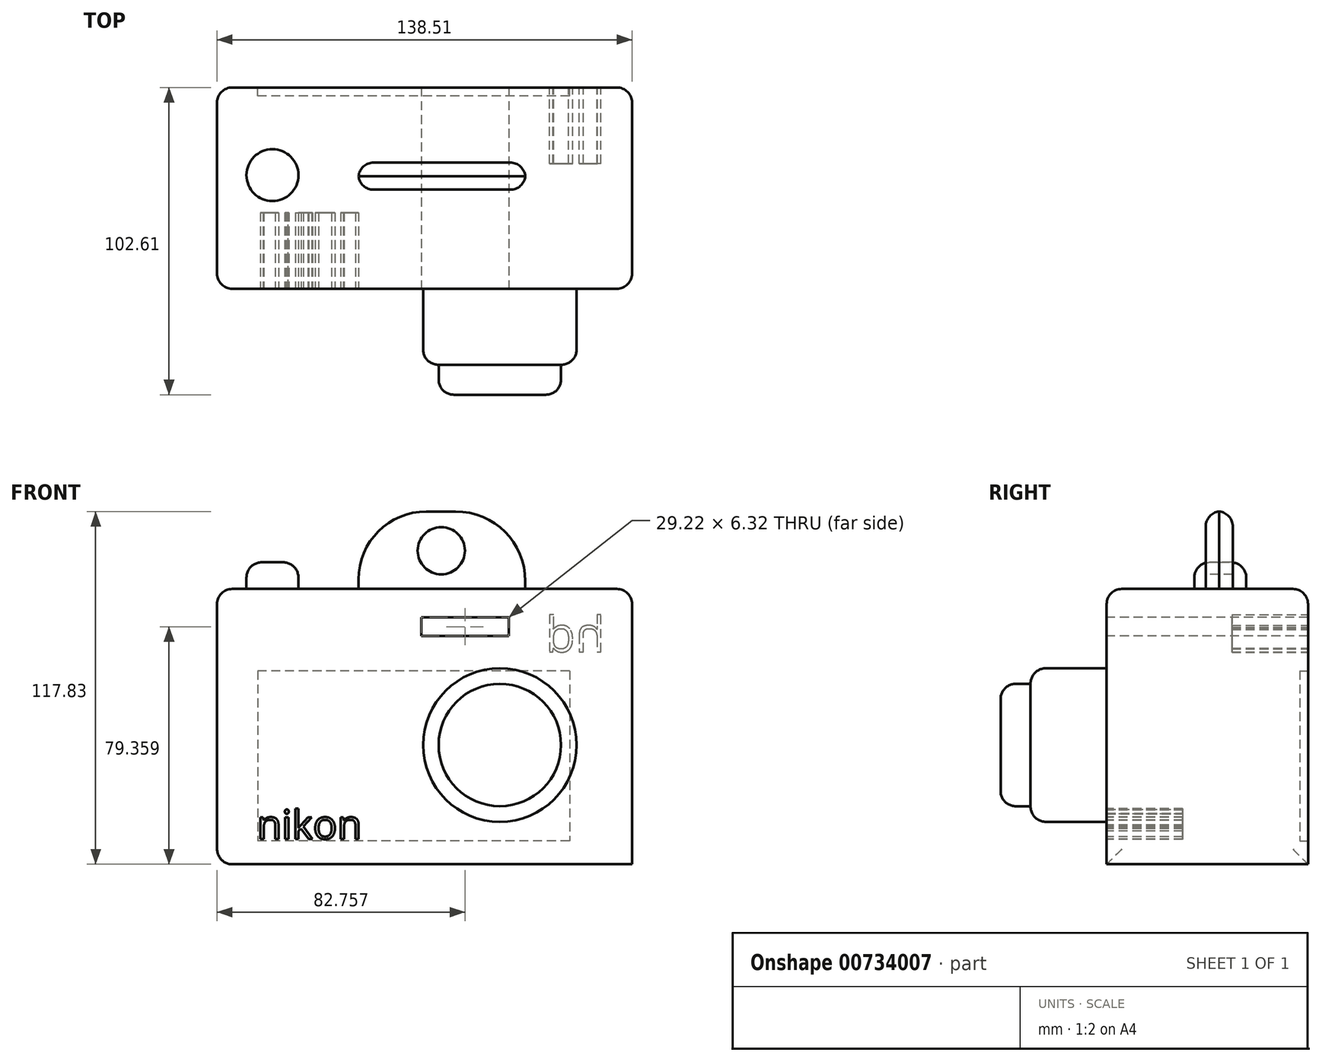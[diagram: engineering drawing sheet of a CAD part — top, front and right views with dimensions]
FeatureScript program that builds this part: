
annotation { "Feature Type Name" : "Feature", "Feature Type Description" : "" }
export const myFeature = defineFeature(function(context is Context, id is Id, definition is map)
    precondition{}
    {
        {
            var Q0;
            Q0=qCreatedBy(makeId("Top.planeOp"),FACE);
            var sketch = newSketch(context, id + "F0", { "sketchPlane" : qUnion([Q0])});
            skLineSegment(sketch, "E0.bottom", {"start": v(-117.69, 9.71) * mm, "end": v(20.82, 9.71) * mm});
            skLineSegment(sketch, "E0.top", {"start": v(-117.69, -57.5) * mm, "end": v(20.82, -57.5) * mm});
            skLineSegment(sketch, "E0.left", {"start": v(-117.69, 9.71) * mm, "end": v(-117.69, -57.5) * mm});
            skLineSegment(sketch, "E0.right", {"start": v(20.82, 9.71) * mm, "end": v(20.82, -57.5) * mm});
            skSolve(sketch);
        }
        {
            var Q0;
            Q0 = qSketchRegion(id + "F0", true);
            extrude(context, id + "F1", {"entities" : qUnion([Q0]), "depth" : 91.95 * mm, "offsetDistance" : 25.4 * mm});
        }
        {
            var Q0;
            Q0=makeQuery(id+"F1.opExtrude","SWEPT_FACE",FACE,{"disambiguationData":[OSD([sQuery(id+"F0.wireOp",EDGE,"E0.top")])]});
            var sketch = newSketch(context, id + "F2", { "sketchPlane" : qUnion([Q0])});
            skCircle(sketch, "E1", {"center": v(-23.3, 39.82) * mm, "radius": 25.62 * mm});
            skSolve(sketch);
        }
        {
            var Q0;
            Q0=makeQuery(id+"F2.imprint","IMPRINT",FACE,{"disambiguationData":[TD([[makeQuery(id+"F2.imprint","IMPRINT",EDGE,{"derivedFrom":sQuery(id+"F2.wireOp",EDGE,"E1")}),1.0]])]});
            extrude(context, id + "F3", {"entities" : qUnion([Q0]), "operationType" : NewBodyOperationType.ADD, "depth" : 25.4 * mm, "offsetDistance" : 25.4 * mm});
        }
        {
            var Q0;
            Q0=makeQuery(id+"F3.opExtrude","CAP_FACE",FACE,{"disambiguationData":[OSD([sQuery(id+"F2.wireOp",EDGE,"E1")])],"isStart":false});
            var sketch = newSketch(context, id + "F4", { "sketchPlane" : qUnion([Q0])});
            skCircle(sketch, "E2", {"center": v(-23.3, 39.82) * mm, "radius": 20.43 * mm});
            skSolve(sketch);
        }
        {
            var Q0;
            Q0=makeQuery(id+"F4.imprint","IMPRINT",FACE,{"disambiguationData":[TD([[makeQuery(id+"F4.imprint","IMPRINT",EDGE,{"derivedFrom":sQuery(id+"F4.wireOp",EDGE,"E2")}),1.0]])]});
            extrude(context, id + "F5", {"entities" : qUnion([Q0]), "operationType" : NewBodyOperationType.ADD, "depth" : 10 * mm, "offsetDistance" : 25.4 * mm});
        }
        {
            var Q0;
            Q0=makeQuery(id+"F5.opExtrude","CAP_FACE",FACE,{"disambiguationData":[OSD([sQuery(id+"F4.wireOp",EDGE,"E2")])],"isStart":false});
            var Q1;
            Q1=makeQuery(id+"F1.opExtrude","CAP_EDGE",EDGE,{"disambiguationData":[OSD([sQuery(id+"F0.wireOp",EDGE,"E0.right")])],"isStart":false});
            var Q2;
            Q2=makeQuery(id+"F1.opExtrude","CAP_EDGE",EDGE,{"disambiguationData":[OSD([sQuery(id+"F0.wireOp",EDGE,"E0.left")])],"isStart":false});
            var Q3;
            Q3=makeQuery(id+"F3.opExtrude","CAP_EDGE",EDGE,{"disambiguationData":[OSD([sQuery(id+"F2.wireOp",EDGE,"E1")])],"isStart":false});
            fillet(context, id + "F6", {"entities" : qUnion([Q0, Q1, Q2, Q3]), "radius" : 5.08 * mm, "tangentPropagation" : true, "allowEdgeOverflow" : false});
        }
        {
            var Q0;
            Q0=makeQuery(id+"F1.opExtrude","SWEPT_FACE",FACE,{"disambiguationData":[OSD([sQuery(id+"F0.wireOp",EDGE,"E0.left")])]});
            fillet(context, id + "F7", {"entities" : qUnion([Q0]), "radius" : 5.08 * mm, "tangentPropagation" : true, "allowEdgeOverflow" : false});
        }
        {
            var Q0;
            Q0=makeQuery(id+"F1.opExtrude","CAP_FACE",FACE,{"disambiguationData":[OSD([sQuery(id+"F0.wireOp",EDGE,"E0.bottom"),sQuery(id+"F0.wireOp",EDGE,"E0.top"),sQuery(id+"F0.wireOp",EDGE,"E0.left"),sQuery(id+"F0.wireOp",EDGE,"E0.right")])],"isStart":false});
            var sketch = newSketch(context, id + "F8", { "sketchPlane" : qUnion([Q0])});
            skCircle(sketch, "E3", {"center": v(-99.2, -19.58) * mm, "radius": 8.67 * mm});
            skSolve(sketch);
        }
        {
            var Q0;
            Q0=makeQuery(id+"F8.imprint","IMPRINT",FACE,{"disambiguationData":[TD([[makeQuery(id+"F8.imprint","IMPRINT",EDGE,{"derivedFrom":sQuery(id+"F8.wireOp",EDGE,"E3")}),1.0]])]});
            extrude(context, id + "F9", {"entities" : qUnion([Q0]), "operationType" : NewBodyOperationType.ADD, "depth" : 8.9 * mm, "offsetDistance" : 25.4 * mm});
        }
        {
            var Q0;
            Q0=makeQuery(id+"F1.opExtrude","SWEPT_FACE",FACE,{"disambiguationData":[OSD([sQuery(id+"F0.wireOp",EDGE,"E0.top")])]});
            var sketch = newSketch(context, id + "F10", { "sketchPlane" : qUnion([Q0])});
            skText(sketch, "E4", { "text": "nikon", "fontName": "OpenSans-Regular.ttf"});
            const initialGuessF10  = {"E4": [-0.10433, 0.00846, 1, 0, 0.00965]};
            skSetInitialGuess(sketch, initialGuessF10);
            skSolve(sketch);
        }
        {
            var Q0;
            Q0=makeQuery(id+"F10.imprint","IMPRINT",FACE,{"disambiguationData":[TD([[makeQuery(id+"F10.imprint","IMPRINT",EDGE,{"derivedFrom":sQuery(id+"F10.wireOp",EDGE,"E4.sketch_text.stroke-0")}),1.0]])]});
            var sketch = newSketch(context, id + "F11", { "sketchPlane" : qUnion([Q0])});
            skLineSegment(sketch, "E5.bottom", {"start": v(-49.54, 82.52) * mm, "end": v(-20.32, 82.52) * mm});
            skLineSegment(sketch, "E5.top", {"start": v(-49.54, 76.2) * mm, "end": v(-20.32, 76.2) * mm});
            skLineSegment(sketch, "E5.left", {"start": v(-49.54, 82.52) * mm, "end": v(-49.54, 76.2) * mm});
            skLineSegment(sketch, "E5.right", {"start": v(-20.32, 82.52) * mm, "end": v(-20.32, 76.2) * mm});
            skSolve(sketch);
        }
        {
            var Q0;
            Q0=makeQuery(id+"F11.imprint","IMPRINT",FACE,{"disambiguationData":[TD([[makeQuery(id+"F11.imprint","IMPRINT",EDGE,{"derivedFrom":sQuery(id+"F11.wireOp",EDGE,"E5.bottom")}),-1.0]])]});
            var Q1;
            Q1 = qSketchRegion(id + "F10", true);
            extrude(context, id + "F12", {"entities" : qUnion([Q0, Q1]), "operationType" : NewBodyOperationType.REMOVE, "oppositeDirection" : true, "depth" : 25.4 * mm, "offsetDistance" : 25.4 * mm});
        }
        {
            var Q0;
            Q0=makeQuery(id+"F12.boolean.opBoolean","COPY",FACE,{"derivedFrom":makeQuery(id+"F12.opExtrude","CAP_FACE",FACE,{"disambiguationData":[OSD([sQuery(id+"F11.wireOp",EDGE,"E5.bottom"),sQuery(id+"F11.wireOp",EDGE,"E5.top"),sQuery(id+"F11.wireOp",EDGE,"E5.left"),sQuery(id+"F11.wireOp",EDGE,"E5.right")])],"isStart":false})});
            extrude(context, id + "F13", {"entities" : qUnion([Q0]), "operationType" : NewBodyOperationType.REMOVE, "oppositeDirection" : true, "depth" : 25.4 * mm, "offsetDistance" : 25.4 * mm});
        }
        {
            var Q0;
            Q0=makeQuery(id+"F13.boolean.opBoolean","COPY",FACE,{"derivedFrom":makeQuery(id+"F13.opExtrude","CAP_FACE",FACE,{"disambiguationData":[OSD([sQuery(id+"F11.wireOp",EDGE,"E5.bottom"),sQuery(id+"F11.wireOp",EDGE,"E5.top"),sQuery(id+"F11.wireOp",EDGE,"E5.left"),sQuery(id+"F11.wireOp",EDGE,"E5.right")])],"isStart":false})});
            extrude(context, id + "F14", {"entities" : qUnion([Q0]), "operationType" : NewBodyOperationType.REMOVE, "oppositeDirection" : true, "depth" : 25.4 * mm, "offsetDistance" : 25.4 * mm});
        }
        {
            var Q0;
            Q0=makeQuery(id+"F1.opExtrude","SWEPT_FACE",FACE,{"disambiguationData":[OSD([sQuery(id+"F0.wireOp",EDGE,"E0.bottom")])]});
            var sketch = newSketch(context, id + "F15", { "sketchPlane" : qUnion([Q0])});
            skText(sketch, "E6", { "text": "hd", "fontName": "OpenSans-Regular.ttf"});
            const initialGuessF15  = {"E6": [-0.01188, 0.07097, 1, 0, 0.0117]};
            skSetInitialGuess(sketch, initialGuessF15);
            skSolve(sketch);
        }
        {
            var Q0;
            Q0 = qSketchRegion(id + "F15", true);
            extrude(context, id + "F16", {"entities" : qUnion([Q0]), "operationType" : NewBodyOperationType.REMOVE, "oppositeDirection" : true, "depth" : 25.4 * mm, "offsetDistance" : 25.4 * mm});
        }
        {
            var Q0;
            {var subQ2=sQuery(id+"F0.wireOp",EDGE,"E0.bottom");var subQ3=makeQuery(id+"F1.opExtrude","SWEPT_FACE",FACE,{"disambiguationData":[OSD([subQ2])]});var subQ4=sQuery(id+"F0.wireOp",EDGE,"E0.left");Q0=makeQuery(id+"F16.boolean.opBoolean","SPLIT",FACE,{"disambiguationData":[TD([makeQuery(id+"F7.opFillet","BLEND_FACE",FACE,{"disambiguationData":[OSD([subQ4])]})])],"derivedFrom":subQ3});}
            var sketch = newSketch(context, id + "F17", { "sketchPlane" : qUnion([Q0])});
            skLineSegment(sketch, "E7.bottom", {"start": v(0, 64.63) * mm, "end": v(104.1, 64.63) * mm});
            skLineSegment(sketch, "E7.top", {"start": v(0, 7.8) * mm, "end": v(104.1, 7.8) * mm});
            skLineSegment(sketch, "E7.left", {"start": v(0, 64.63) * mm, "end": v(0, 7.8) * mm});
            skLineSegment(sketch, "E7.right", {"start": v(104.1, 64.63) * mm, "end": v(104.1, 7.8) * mm});
            skSolve(sketch);
        }
        {
            var Q0;
            Q0 = qSketchRegion(id + "F17", true);
            extrude(context, id + "F18", {"entities" : qUnion([Q0]), "operationType" : NewBodyOperationType.REMOVE, "oppositeDirection" : true, "depth" : 2.8 * mm, "offsetDistance" : 25.4 * mm});
        }
        {
            var Q0;
            Q0=makeQuery(id+"F1.opExtrude","CAP_FACE",FACE,{"disambiguationData":[OSD([sQuery(id+"F0.wireOp",EDGE,"E0.bottom"),sQuery(id+"F0.wireOp",EDGE,"E0.top"),sQuery(id+"F0.wireOp",EDGE,"E0.left"),sQuery(id+"F0.wireOp",EDGE,"E0.right")])],"isStart":false});
            var sketch = newSketch(context, id + "F19", { "sketchPlane" : qUnion([Q0])});
            skLineSegment(sketch, "E8.bottom", {"start": v(-70.5, -15.4) * mm, "end": v(-14.75, -15.4) * mm});
            skLineSegment(sketch, "E8.top", {"start": v(-70.5, -24.44) * mm, "end": v(-14.75, -24.44) * mm});
            skLineSegment(sketch, "E8.left", {"start": v(-70.5, -15.4) * mm, "end": v(-70.5, -24.44) * mm});
            skLineSegment(sketch, "E8.right", {"start": v(-14.75, -15.4) * mm, "end": v(-14.75, -24.44) * mm});
            skSolve(sketch);
        }
        {
            var Q0;
            Q0 = qSketchRegion(id + "F19", true);
            extrude(context, id + "F20", {"entities" : qUnion([Q0]), "operationType" : NewBodyOperationType.ADD, "depth" : 25.9 * mm, "offsetDistance" : 25.4 * mm});
        }
        {
            var Q0;
            Q0=makeQuery(id+"F20.opExtrude","CAP_EDGE",EDGE,{"disambiguationData":[OSD([sQuery(id+"F19.wireOp",EDGE,"E8.left")])],"isStart":false});
            fillet(context, id + "F21", {"entities" : qUnion([Q0]), "radius" : 22.7 * mm, "tangentPropagation" : true, "allowEdgeOverflow" : false});
        }
        {
            var Q0;
            Q0=makeQuery(id+"F20.opExtrude","CAP_EDGE",EDGE,{"disambiguationData":[OSD([sQuery(id+"F19.wireOp",EDGE,"E8.right")])],"isStart":false});
            fillet(context, id + "F22", {"entities" : qUnion([Q0]), "radius" : 23.3 * mm, "tangentPropagation" : true, "allowEdgeOverflow" : false});
        }
        {
            var Q0;
            Q0=makeQuery(id+"F20.opExtrude","SWEPT_FACE",FACE,{"disambiguationData":[OSD([sQuery(id+"F19.wireOp",EDGE,"E8.top")])]});
            var sketch = newSketch(context, id + "F23", { "sketchPlane" : qUnion([Q0])});
            skCircle(sketch, "E9", {"center": v(-42.83, 104.72) * mm, "radius": 7.88 * mm});
            skSolve(sketch);
        }
        {
            var Q0;
            Q0 = qSketchRegion(id + "F23", true);
            extrude(context, id + "F24", {"entities" : qUnion([Q0]), "operationType" : NewBodyOperationType.REMOVE, "oppositeDirection" : true, "depth" : 45.97 * mm, "offsetDistance" : 25.4 * mm});
        }
        {
            var Q0;
            Q0=makeQuery(id+"F21.opFillet","BLEND_EDGE",EDGE,{"blendedFrom":[makeQuery(id+"F20.opExtrude","CAP_EDGE",EDGE,{"disambiguationData":[OSD([sQuery(id+"F19.wireOp",EDGE,"E8.left")])],"isStart":false}),makeQuery(id+"F20.opExtrude","SWEPT_FACE",FACE,{"disambiguationData":[OSD([sQuery(id+"F19.wireOp",EDGE,"E8.top")])]})],"blendedInto":[makeQuery(id+"F20.opExtrude","SWEPT_FACE",FACE,{"disambiguationData":[OSD([sQuery(id+"F19.wireOp",EDGE,"E8.top")])]})]});
            var Q1;
            Q1=makeQuery(id+"F21.opFillet","BLEND_EDGE",EDGE,{"blendedFrom":[makeQuery(id+"F20.opExtrude","CAP_EDGE",EDGE,{"disambiguationData":[OSD([sQuery(id+"F19.wireOp",EDGE,"E8.left")])],"isStart":false}),makeQuery(id+"F20.opExtrude","SWEPT_FACE",FACE,{"disambiguationData":[OSD([sQuery(id+"F19.wireOp",EDGE,"E8.bottom")])]})],"blendedInto":[makeQuery(id+"F20.opExtrude","SWEPT_FACE",FACE,{"disambiguationData":[OSD([sQuery(id+"F19.wireOp",EDGE,"E8.bottom")])]})]});
            fillet(context, id + "F25", {"entities" : qUnion([Q0, Q1]), "radius" : 5.08 * mm, "tangentPropagation" : true, "allowEdgeOverflow" : false});
        }
        {
            var Q0;
            Q0=makeQuery(id+"F9.opExtrude","CAP_EDGE",EDGE,{"disambiguationData":[OSD([sQuery(id+"F8.wireOp",EDGE,"E3")])],"isStart":false});
            fillet(context, id + "F26", {"entities" : qUnion([Q0]), "radius" : 5.08 * mm, "tangentPropagation" : true, "allowEdgeOverflow" : false});
        }
    });
